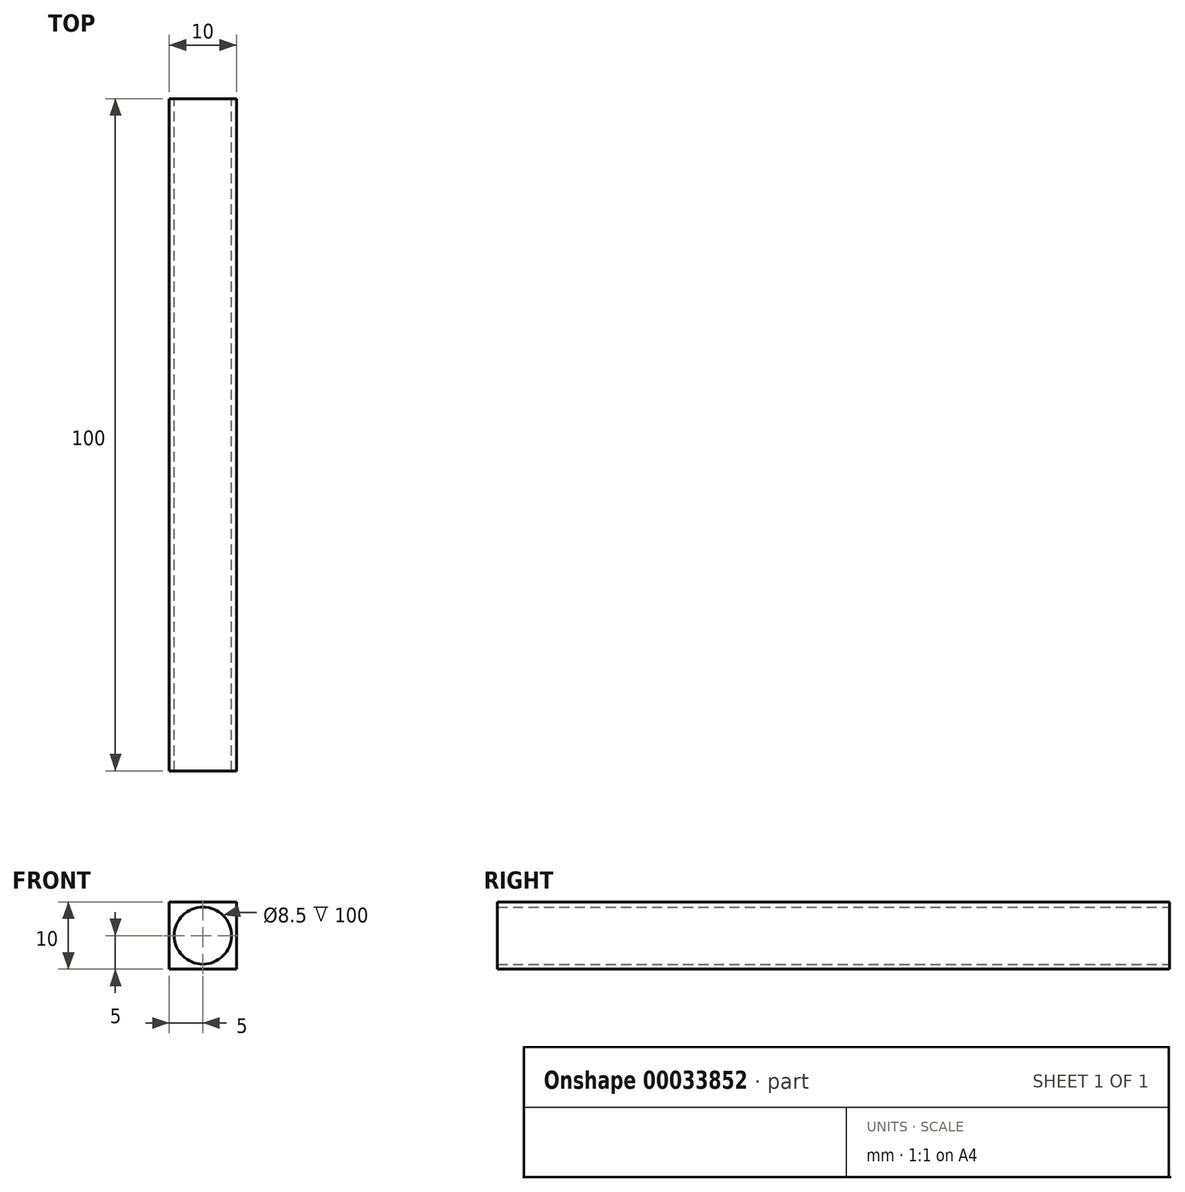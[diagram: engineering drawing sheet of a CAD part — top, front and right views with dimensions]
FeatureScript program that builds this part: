
annotation { "Feature Type Name" : "Feature", "Feature Type Description" : "" }
export const myFeature = defineFeature(function(context is Context, id is Id, definition is map)
    precondition{}
    {
        {
            var Q0;
            Q0=qCreatedBy(makeId("Front.planeOp"),FACE);
            var sketch = newSketch(context, id + "F0", { "sketchPlane" : qUnion([Q0])});
            skCircle(sketch, "E0", {"center": v(0, 0) * mm, "radius": 4.25 * mm});
            skLineSegment(sketch, "E1.rect.bottom", {"start": v(4.5, -5) * mm, "end": v(-4.5, -5) * mm});
            skLineSegment(sketch, "E1.rect.top", {"start": v(4.5, 5) * mm, "end": v(-4.5, 5) * mm});
            skLineSegment(sketch, "E1.rect.left", {"start": v(5, -4.5) * mm, "end": v(5, 4.5) * mm});
            skLineSegment(sketch, "E1.rect.right", {"start": v(-5, -4.5) * mm, "end": v(-5, 4.5) * mm});
            skPoint(sketch, "E2.visualSharp", {"position": v(-5, 5) * mm});
            skPoint(sketch, "E3.visualSharp", {"position": v(5, 5) * mm});
            skPoint(sketch, "E4.visualSharp", {"position": v(-5, -5) * mm});
            skPoint(sketch, "E5.visualSharp", {"position": v(5, -5) * mm});
            skLineSegment(sketch, "E6", {"start": v(-4.5, 5) * mm, "end": v(-5, 5) * mm});
            skLineSegment(sketch, "E7", {"start": v(-5, 4.5) * mm, "end": v(-5, 5) * mm});
            skLineSegment(sketch, "E8", {"start": v(4.5, 5) * mm, "end": v(5, 5) * mm});
            skLineSegment(sketch, "E9", {"start": v(5, 5) * mm, "end": v(5, 4.5) * mm});
            skLineSegment(sketch, "E10", {"start": v(5, -4.5) * mm, "end": v(5, -5) * mm});
            skLineSegment(sketch, "E11", {"start": v(4.5, -5) * mm, "end": v(5, -5) * mm});
            skLineSegment(sketch, "E12", {"start": v(-5, -5) * mm, "end": v(-4.5, -5) * mm});
            skLineSegment(sketch, "E13", {"start": v(-5, -4.5) * mm, "end": v(-5, -5) * mm});
            skSolve(sketch);
        }
        {
            var Q0;
            Q0=makeQuery(id+"F0.imprint","IMPRINT",FACE,{"disambiguationData":[TD([[makeQuery(id+"F0.imprint","IMPRINT",EDGE,{"derivedFrom":sQuery(id+"F0.wireOp",EDGE,"E0")}),-1.0]])]});
            extrude(context, id + "F1", {"entities" : qUnion([Q0]), "depth" : 100 * mm});
        }
    });
